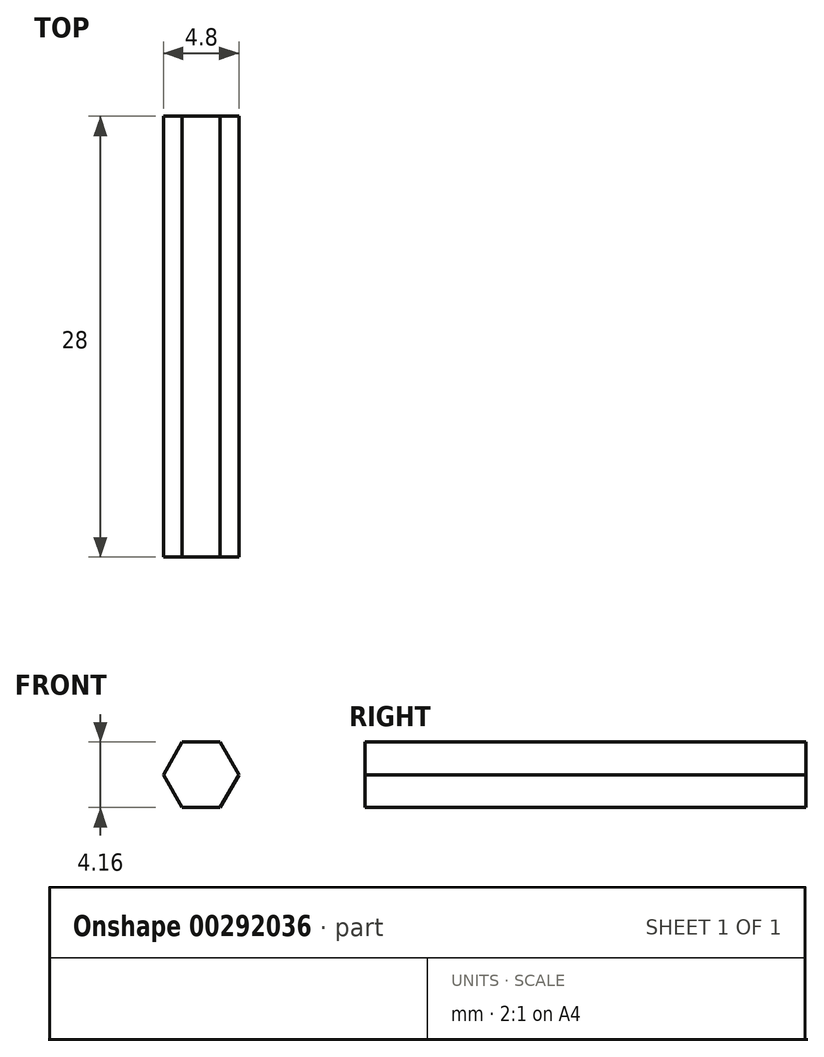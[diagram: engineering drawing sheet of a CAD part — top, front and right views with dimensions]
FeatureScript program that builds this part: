
annotation { "Feature Type Name" : "Feature", "Feature Type Description" : "" }
export const myFeature = defineFeature(function(context is Context, id is Id, definition is map)
    precondition{}
    {
        {
            var Q0;
            Q0=qCreatedBy(makeId("Front.planeOp"),FACE);
            var sketch = newSketch(context, id + "F0", { "sketchPlane" : qUnion([Q0])});
            skCircle(sketch, "E0.cCircle", {"center": v(0, 0) * mm, "radius": 11.51 * mm, "construction": true});
            skLineSegment(sketch, "E0.0", {"start": v(-6.65, 11.51) * mm, "end": v(6.65, 11.51) * mm});
            skLineSegment(sketch, "E0.1", {"start": v(6.65, 11.51) * mm, "end": v(13.3, 0) * mm});
            skLineSegment(sketch, "E0.2", {"start": v(13.3, 0) * mm, "end": v(6.65, -11.51) * mm});
            skLineSegment(sketch, "E0.3", {"start": v(6.65, -11.51) * mm, "end": v(-6.65, -11.51) * mm});
            skLineSegment(sketch, "E0.4", {"start": v(-6.65, -11.51) * mm, "end": v(-13.3, 0) * mm});
            skLineSegment(sketch, "E0.5", {"start": v(-13.3, 0) * mm, "end": v(-6.65, 11.51) * mm});
            skPoint(sketch, "E0.0.midPoint", {"position": v(0, 11.51) * mm});
            skSolve(sketch);
        }
        {
            var Q0;
            Q0 = qSketchRegion(id + "F0", true);
            extrude(context, id + "F1", {"entities" : qUnion([Q0]), "depth" : 28 * mm});
        }
        {
            var Q0;
            Q0=makeQuery(id+"F1.opExtrude","SWEPT_BODY",BODY,{"disambiguationData":[OSD([sQuery(id+"F0.wireOp",EDGE,"E0.0"),sQuery(id+"F0.wireOp",EDGE,"E0.1"),sQuery(id+"F0.wireOp",EDGE,"E0.2"),sQuery(id+"F0.wireOp",EDGE,"E0.3"),sQuery(id+"F0.wireOp",EDGE,"E0.4"),sQuery(id+"F0.wireOp",EDGE,"E0.5")])]});
            deleteBodies(context, id + "F2", {"entities" : qUnion([Q0])});
        }
        {
            var Q0;
            Q0=qCreatedBy(makeId("Front.planeOp"),FACE);
            var sketch = newSketch(context, id + "F3", { "sketchPlane" : qUnion([Q0])});
            skCircle(sketch, "E1.cCircle", {"center": v(0, 0) * mm, "radius": 2.08 * mm, "construction": true});
            skLineSegment(sketch, "E1.0", {"start": v(-1.2, 2.08) * mm, "end": v(1.2, 2.08) * mm});
            skLineSegment(sketch, "E1.1", {"start": v(1.2, 2.08) * mm, "end": v(2.4, 0) * mm});
            skLineSegment(sketch, "E1.2", {"start": v(2.4, 0) * mm, "end": v(1.2, -2.08) * mm});
            skLineSegment(sketch, "E1.3", {"start": v(1.2, -2.08) * mm, "end": v(-1.2, -2.08) * mm});
            skLineSegment(sketch, "E1.4", {"start": v(-1.2, -2.08) * mm, "end": v(-2.4, 0) * mm});
            skLineSegment(sketch, "E1.5", {"start": v(-2.4, 0) * mm, "end": v(-1.2, 2.08) * mm});
            skPoint(sketch, "E1.0.midPoint", {"position": v(0, 2.08) * mm});
            skSolve(sketch);
        }
        {
            var Q0;
            Q0 = qSketchRegion(id + "F3", true);
            extrude(context, id + "F4", {"entities" : qUnion([Q0]), "depth" : 28 * mm});
        }
    });
